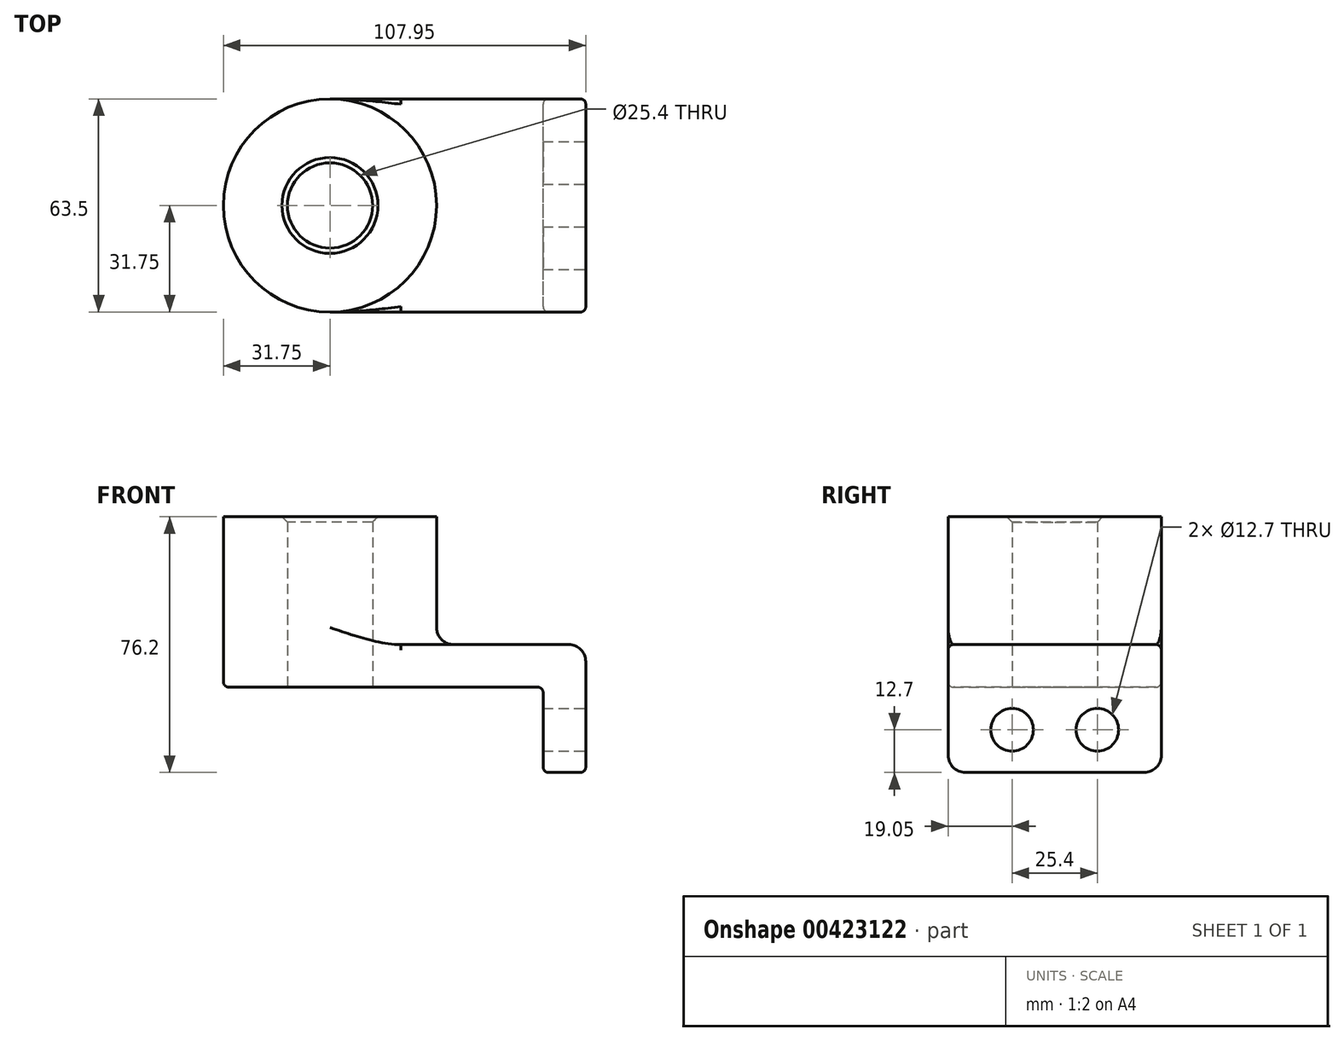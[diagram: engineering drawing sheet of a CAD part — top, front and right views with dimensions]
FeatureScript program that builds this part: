
annotation { "Feature Type Name" : "Feature", "Feature Type Description" : "" }
export const myFeature = defineFeature(function(context is Context, id is Id, definition is map)
    precondition{}
    {
        {
            var Q0;
            Q0=qCreatedBy(makeId("Top.planeOp"),FACE);
            var sketch = newSketch(context, id + "F0", { "sketchPlane" : qUnion([Q0])});
            skLineSegment(sketch, "E0.bottom", {"start": v(38.1, -31.75) * mm, "end": v(-38.1, -31.75) * mm});
            skLineSegment(sketch, "E0.top", {"start": v(38.1, 31.75) * mm, "end": v(-38.1, 31.75) * mm});
            skLineSegment(sketch, "E0.left", {"start": v(38.1, -31.75) * mm, "end": v(38.1, 31.75) * mm});
            skLineSegment(sketch, "E0.right", {"start": v(-38.1, -31.75) * mm, "end": v(-38.1, 31.75) * mm});
            skPoint(sketch, "E0.middle", {"position": v(0, 0) * mm});
            skCircle(sketch, "E1", {"center": v(-38.1, 0) * mm, "radius": 31.75 * mm});
            skCircle(sketch, "E2", {"center": v(-38.1, 0) * mm, "radius": 12.7 * mm});
            skSolve(sketch);
        }
        {
            var Q0;
            Q0 = qSketchRegion(id + "F0", true);
            extrude(context, id + "F1", {"entities" : qUnion([Q0]), "depth" : 12.7 * mm});
        }
        {
            var Q0;
            {var subQ1=sQuery(id+"F0.wireOp",EDGE,"E0.right");var subQ3=sQuery(id+"F0.wireOp",EDGE,"E2");var subQ4=makeQuery(id+"F0.imprint","INTERSECT",VERTEX,{"disambiguationData":[OD(0.0)],"derivedFrom":[subQ1,subQ3]});Q0=makeQuery(id+"F0.imprint","IMPRINT",FACE,{"disambiguationData":[TD([[makeQuery(id+"F0.imprint","IMPRINT",EDGE,{"disambiguationData":[TD([[subQ4,1.0]])],"derivedFrom":subQ3}),-1.0]])]});}
            var Q1;
            {var subQ1=sQuery(id+"F0.wireOp",EDGE,"E0.right");var subQ3=sQuery(id+"F0.wireOp",EDGE,"E2");var subQ4=makeQuery(id+"F0.imprint","INTERSECT",VERTEX,{"disambiguationData":[OD(0.0)],"derivedFrom":[subQ1,subQ3]});Q1=makeQuery(id+"F0.imprint","IMPRINT",FACE,{"disambiguationData":[TD([[makeQuery(id+"F0.imprint","IMPRINT",EDGE,{"disambiguationData":[TD([[subQ4,-1.0]])],"derivedFrom":subQ3}),-1.0]])]});}
            extrude(context, id + "F2", {"entities" : qUnion([Q0, Q1]), "operationType" : NewBodyOperationType.ADD, "depth" : 50.8 * mm});
        }
        {
            var Q0;
            Q0=makeQuery(id+"F1.opExtrude","SWEPT_FACE",FACE,{"disambiguationData":[OSD([sQuery(id+"F0.wireOp",EDGE,"E0.left")])]});
            var sketch = newSketch(context, id + "F3", { "sketchPlane" : qUnion([Q0])});
            skLineSegment(sketch, "E3.bottom", {"start": v(-31.75, 12.7) * mm, "end": v(31.75, 12.7) * mm});
            skLineSegment(sketch, "E3.top", {"start": v(-31.75, -25.4) * mm, "end": v(31.75, -25.4) * mm});
            skLineSegment(sketch, "E3.left", {"start": v(-31.75, 12.7) * mm, "end": v(-31.75, -25.4) * mm});
            skLineSegment(sketch, "E3.right", {"start": v(31.75, 12.7) * mm, "end": v(31.75, -25.4) * mm});
            skCircle(sketch, "E4", {"center": v(-12.7, -12.7) * mm, "radius": 6.35 * mm});
            skLineSegment(sketch, "E5", {"start": v(0, 0) * mm, "end": v(0, -25.4) * mm, "construction": true});
            skCircle(sketch, "E6.MirrorC", {"center": v(12.7, -12.7) * mm, "radius": 6.35 * mm});
            skSolve(sketch);
        }
        {
            var Q0;
            Q0 = qSketchRegion(id + "F3", true);
            extrude(context, id + "F4", {"entities" : qUnion([Q0]), "operationType" : NewBodyOperationType.ADD, "oppositeDirection" : true, "depth" : 12.7 * mm});
        }
        {
            var Q0;
            {var subQ0=sQuery(id+"F0.wireOp",EDGE,"E1");Q0=makeQuery(id+"F2.boolean.opBoolean","INTERSECT",EDGE,{"derivedFrom":[makeQuery(id+"F1.opExtrude","CAP_FACE",FACE,{"disambiguationData":[OSD([sQuery(id+"F0.wireOp",EDGE,"E0.bottom"),sQuery(id+"F0.wireOp",EDGE,"E0.top"),sQuery(id+"F0.wireOp",EDGE,"E0.left"),subQ0,sQuery(id+"F0.wireOp",EDGE,"E2")])],"isStart":false}),makeQuery(id+"F2.opExtrude","SWEPT_FACE",FACE,{"disambiguationData":[OSD([subQ0])]})]});}
            var Q1;
            Q1=makeQuery(id+"F1.opExtrude","CAP_EDGE",EDGE,{"disambiguationData":[OSD([sQuery(id+"F0.wireOp",EDGE,"E0.left")])],"isStart":false});
            var Q2;
            Q2=makeQuery(id+"F4.opExtrude","SWEPT_EDGE",EDGE,{"disambiguationData":[OSD([sQuery(id+"F3.wireOp",EDGE,"E3.top"),sQuery(id+"F3.wireOp",EDGE,"E3.left")])]});
            var Q3;
            Q3=makeQuery(id+"F4.opExtrude","SWEPT_EDGE",EDGE,{"disambiguationData":[OSD([sQuery(id+"F3.wireOp",EDGE,"E3.top"),sQuery(id+"F3.wireOp",EDGE,"E3.right")])]});
            fillet(context, id + "F5", {"entities" : qUnion([Q0, Q1, Q2, Q3]), "radius" : 5.08 * mm, "tangentPropagation" : true, "allowEdgeOverflow" : false});
        }
        {
            var Q0;
            Q0=makeQuery(id+"F1.opExtrude","CAP_EDGE",EDGE,{"disambiguationData":[OSD([sQuery(id+"F0.wireOp",EDGE,"E0.bottom")])],"isStart":true});
            var Q1;
            Q1=makeQuery(id+"F4.opExtrude","CAP_EDGE",EDGE,{"disambiguationData":[OSD([sQuery(id+"F3.wireOp",EDGE,"E3.left")])],"isStart":false});
            var Q2;
            Q2=makeQuery(id+"F4.boolean.opBoolean","INTERSECT",EDGE,{"derivedFrom":[makeQuery(id+"F1.opExtrude","CAP_FACE",FACE,{"disambiguationData":[OSD([sQuery(id+"F0.wireOp",EDGE,"E0.bottom"),sQuery(id+"F0.wireOp",EDGE,"E0.top"),sQuery(id+"F0.wireOp",EDGE,"E0.left"),sQuery(id+"F0.wireOp",EDGE,"E1"),sQuery(id+"F0.wireOp",EDGE,"E2")])],"isStart":true}),makeQuery(id+"F4.opExtrude","CAP_FACE",FACE,{"disambiguationData":[OSD([sQuery(id+"F3.wireOp",EDGE,"E3.bottom"),sQuery(id+"F3.wireOp",EDGE,"E3.top"),sQuery(id+"F3.wireOp",EDGE,"E3.left"),sQuery(id+"F3.wireOp",EDGE,"E3.right"),sQuery(id+"F3.wireOp",EDGE,"E4"),sQuery(id+"F3.wireOp",EDGE,"E6.MirrorC")])],"isStart":false})]});
            var Q3;
            Q3=makeQuery(id+"F4.boolean.opBoolean","MERGE",EDGE,{"derivedFrom":[makeQuery(id+"F1.opExtrude","SWEPT_EDGE",EDGE,{"disambiguationData":[OSD([sQuery(id+"F0.wireOp",EDGE,"E0.bottom"),sQuery(id+"F0.wireOp",EDGE,"E0.left")])]}),makeQuery(id+"F4.opExtrude","CAP_EDGE",EDGE,{"disambiguationData":[OSD([sQuery(id+"F3.wireOp",EDGE,"E3.left")])],"isStart":true})]});
            fillet(context, id + "F6", {"entities" : qUnion([Q0, Q1, Q2, Q3]), "radius" : 1.59 * mm, "tangentPropagation" : true, "allowEdgeOverflow" : false});
        }
        {
            var Q0;
            Q0=makeQuery(id+"F2.opExtrude","CAP_EDGE",EDGE,{"disambiguationData":[OSD([sQuery(id+"F0.wireOp",EDGE,"E2")])],"isStart":false});
            chamfer(context, id + "F7", {"entities" : qUnion([Q0]), "width" : 1.59 * mm, "tangentPropagation" : true});
        }
    });
